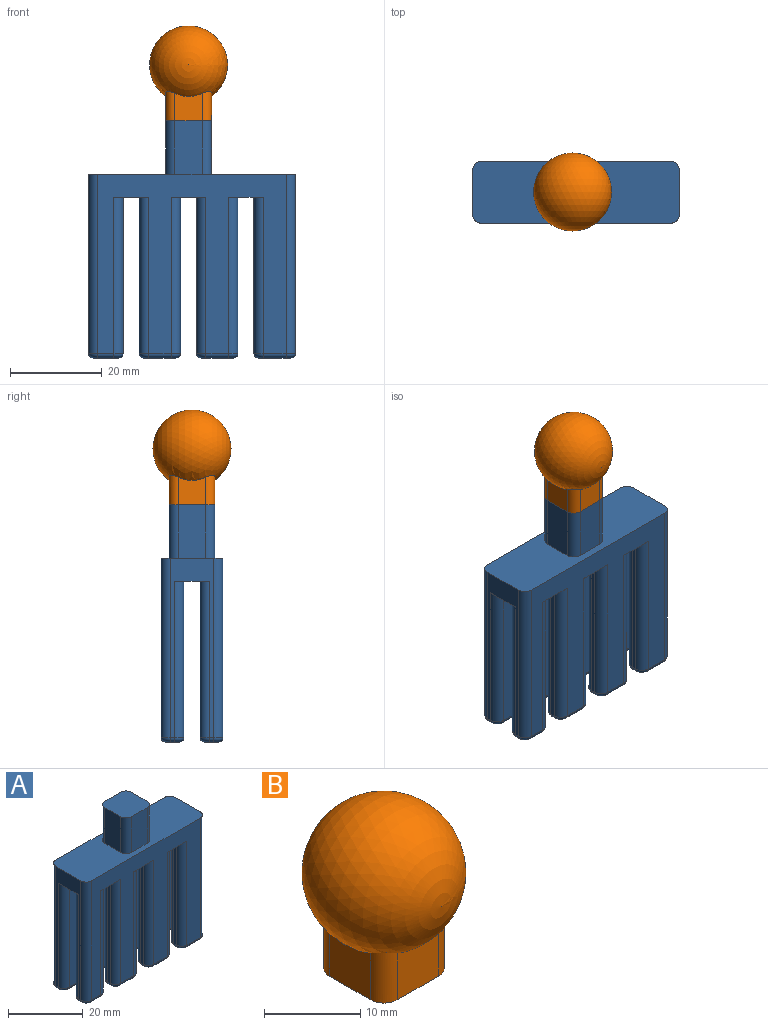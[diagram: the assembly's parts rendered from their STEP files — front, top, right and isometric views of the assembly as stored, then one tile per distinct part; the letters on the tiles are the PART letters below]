
ASSEMBLY  parts=2 mates=1
PART A: 139 faces, bbox 45.3x13.8x51.7 mm
  f0: plane 34x1mm, normal (-1,0,0), area 34mm2, adj f5,f26,f67,f92
  f1: plane 34x1mm, normal (-1,0,0), area 34mm2, adj f7,f26,f74,f77
  f2: plane 34x1mm, normal (1,0,0), area 34mm2, adj f4,f26,f65,f101
  f3: plane 34x1mm, normal (1,0,0), area 34mm2, adj f6,f26,f70,f84
  f4: cylinder r=2mm len=34mm, axis (0,0,1), area 106.8mm2, adj f2,f22,f26,f99
  f5: cylinder r=2mm len=34mm, axis (0,0,-1), area 106.8mm2, adj f0,f22,f26,f91
  f6: cylinder r=2mm len=34mm, axis (0,0,-1), area 106.8mm2, adj f3,f17,f26,f83
  f7: cylinder r=2mm len=34mm, axis (0,0,1), area 106.8mm2, adj f1,f17,f26,f75
  f8: plane 11.69x6mm, normal (-1,0,0), area 70.1mm2, adj f11,f14,f25,f32
  f9: plane 11.69x6mm, normal (1,0,0), area 70.1mm2, adj f12,f13,f25,f32
  f10: plane 11.69x6mm, normal (0,1,0), area 70.1mm2, adj f13,f14,f25,f32
  f11: cylinder r=2mm len=11.69mm, axis (0,0,-1), area 36.7mm2, adj f8,f25,f27,f32
  f12: cylinder r=2mm len=11.69mm, axis (0,0,1), area 36.7mm2, adj f9,f25,f27,f32
  f13: cylinder r=2mm len=11.69mm, axis (0,0,-1), area 36.7mm2, adj f9,f10,f25,f32
  f14: cylinder r=2mm len=11.69mm, axis (0,0,1), area 36.7mm2, adj f8,f10,f25,f32
  f15: plane 34x5mm, normal (0,-1,0), area 170mm2, adj f26,f72,f74,f81
  f16: plane 34x1mm, normal (1,0,0), area 34mm2, adj f26,f72,f73,f80
  f17: plane 41x39mm, normal (0,1,0), area 834mm2, adj f6,f7,f25,f26,f52,f53,f60,f62
  f18: plane 34x1mm, normal (-1,0,0), area 34mm2, adj f26,f69,f71,f89
  f19: plane 34x5mm, normal (0,-1,0), area 170mm2, adj f26,f69,f70,f88
  f20: plane 34x1mm, normal (1,0,0), area 34mm2, adj f26,f66,f68,f97
  f21: plane 34x5mm, normal (0,1,0), area 170mm2, adj f26,f66,f67,f96
  f22: plane 41x39mm, normal (0,-1,0), area 834mm2, adj f4,f5,f25,f26,f49,f58,f59,f61
  f23: plane 34x5mm, normal (0,1,0), area 170mm2, adj f26,f63,f65,f105
  f24: plane 34x1mm, normal (-1,0,0), area 34mm2, adj f26,f63,f64,f104
  f25: plane 45x13.5mm, normal (0,0,1), area 507.5mm2, adj f8,f9,f10,f11,f12,f13,f14,f17
  f26: plane 45x13.5mm, normal (0,0,-1), area 286.5mm2, adj f0,f1,f2,f3,f4,f5,f6,f7
  f27: plane 11.69x6mm, normal (0,-1,0), area 70.1mm2, adj f11,f12,f25,f32
  f28: plane 7x3mm, normal (0,0,-1), area 20.1mm2, adj f99,f100,f101,f102,f103,f104,f105,f106
  f29: plane 7x3mm, normal (0,0,-1), area 20.1mm2, adj f91,f92,f93,f94,f95,f96,f97,f98
  f30: plane 7x3mm, normal (0,0,-1), area 20.1mm2, adj f75,f76,f77,f78,f79,f80,f81,f82
  f31: plane 7x3mm, normal (0,0,-1), area 20.1mm2, adj f83,f84,f85,f86,f87,f88,f89,f90
  f32: plane 10x10mm, normal (0,0,1), area 96.6mm2, adj f8,f9,f10,f11,f12,f13,f14,f27
  f33: plane 39x9.5mm, normal (-1,0,0), area 115.5mm2, adj f25,f26,f48,f50,f59,f60,f129,f132
  f34: plane 39x9.5mm, normal (1,0,0), area 115.5mm2, adj f25,f26,f54,f56,f61,f62,f113,f117
  f35: plane 34x1mm, normal (-1,0,0), area 34mm2, adj f26,f57,f58,f108
  f36: plane 34x5mm, normal (0,1,0), area 170mm2, adj f26,f56,f57,f112
  f37: plane 7x3mm, normal (0,0,-1), area 20.1mm2, adj f107,f108,f109,f110,f111,f112,f113,f114
  f38: plane 34x1mm, normal (-1,0,0), area 34mm2, adj f26,f53,f55,f120
  f39: plane 34x5mm, normal (0,-1,0), area 170mm2, adj f26,f54,f55,f116
  f40: plane 7x3mm, normal (0,0,-1), area 20.1mm2, adj f115,f116,f117,f118,f119,f120,f121,f122
  f41: plane 34x1mm, normal (1,0,0), area 34mm2, adj f26,f47,f49,f137
  f42: plane 34x3.5mm, normal (0,1,0), area 119mm2, adj f26,f47,f48,f136
  f43: plane 5.5x3mm, normal (0,0,-1), area 15.6mm2, adj f131,f132,f133,f134,f135,f136,f137,f138
  f44: plane 34x1mm, normal (1,0,0), area 34mm2, adj f26,f51,f52,f124
  f45: plane 34x3.5mm, normal (0,-1,0), area 119mm2, adj f26,f50,f51,f128
  f46: plane 5.5x3mm, normal (0,0,-1), area 15.6mm2, adj f123,f124,f125,f126,f127,f128,f129,f130
  f47: cylinder r=2mm len=34mm, axis (0,0,-1), area 106.8mm2, adj f26,f41,f42,f138
  f48: cylinder r=2mm len=34mm, axis (0,0,1), area 106.8mm2, adj f26,f33,f42,f134
  f49: cylinder r=2mm len=34mm, axis (0,0,1), area 106.8mm2, adj f22,f26,f41,f135
  f50: cylinder r=2mm len=34mm, axis (0,0,-1), area 106.8mm2, adj f26,f33,f45,f130
  f51: cylinder r=2mm len=34mm, axis (0,0,-1), area 106.8mm2, adj f26,f44,f45,f126
  f52: cylinder r=2mm len=34mm, axis (0,0,1), area 106.8mm2, adj f17,f26,f44,f123
  f53: cylinder r=2mm len=34mm, axis (0,0,-1), area 106.8mm2, adj f17,f26,f38,f122
  f54: cylinder r=2mm len=34mm, axis (0,0,-1), area 106.8mm2, adj f26,f34,f39,f115
  f55: cylinder r=2mm len=34mm, axis (0,0,-1), area 106.8mm2, adj f26,f38,f39,f118
  f56: cylinder r=2mm len=34mm, axis (0,0,1), area 106.8mm2, adj f26,f34,f36,f114
  f57: cylinder r=2mm len=34mm, axis (0,0,-1), area 106.8mm2, adj f26,f35,f36,f110
  f58: cylinder r=2mm len=34mm, axis (0,0,-1), area 106.8mm2, adj f22,f26,f35,f107
  f59: cylinder r=2mm len=39mm, axis (0,0,1), area 122.5mm2, adj f22,f25,f33,f131
  f60: cylinder r=2mm len=39mm, axis (0,0,-1), area 122.5mm2, adj f17,f25,f33,f127
  f61: cylinder r=2mm len=39mm, axis (0,0,-1), area 122.5mm2, adj f22,f25,f34,f111
  f62: cylinder r=2mm len=39mm, axis (0,0,1), area 122.5mm2, adj f17,f25,f34,f119
  f63: cylinder r=2mm len=34mm, axis (0,0,1), area 106.8mm2, adj f23,f24,f26,f106
  f64: cylinder r=2mm len=34mm, axis (0,0,1), area 106.8mm2, adj f22,f24,f26,f102
  f65: cylinder r=2mm len=34mm, axis (0,0,1), area 106.8mm2, adj f2,f23,f26,f103
  f66: cylinder r=2mm len=34mm, axis (0,0,1), area 106.8mm2, adj f20,f21,f26,f98
  f67: cylinder r=2mm len=34mm, axis (0,0,1), area 106.8mm2, adj f0,f21,f26,f94
  f68: cylinder r=2mm len=34mm, axis (0,0,-1), area 106.8mm2, adj f20,f22,f26,f95
  f69: cylinder r=2mm len=34mm, axis (0,0,1), area 106.8mm2, adj f18,f19,f26,f90
  f70: cylinder r=2mm len=34mm, axis (0,0,-1), area 106.8mm2, adj f3,f19,f26,f86
  f71: cylinder r=2mm len=34mm, axis (0,0,1), area 106.8mm2, adj f17,f18,f26,f87
  f72: cylinder r=2mm len=34mm, axis (0,0,1), area 106.8mm2, adj f15,f16,f26,f82
  f73: cylinder r=2mm len=34mm, axis (0,0,-1), area 106.8mm2, adj f16,f17,f26,f78
  f74: cylinder r=2mm len=34mm, axis (0,0,-1), area 106.8mm2, adj f1,f15,f26,f79
  f75: torus R=1mm, axis (0,0,1), area 4mm2, adj f7,f30,f76,f77
  f76: cylinder r=1mm len=5mm, axis (-1,0,0), area 7.9mm2, adj f17,f30,f75,f78
  f77: cylinder r=1mm len=1mm, axis (0,-1,0), area 1.6mm2, adj f1,f30,f75,f79
  f78: torus R=1mm, axis (0,0,1), area 4mm2, adj f30,f73,f76,f80
  f79: torus R=1mm, axis (0,0,1), area 4mm2, adj f30,f74,f77,f81
  f80: cylinder r=1mm len=1mm, axis (0,1,0), area 1.6mm2, adj f16,f30,f78,f82
  f81: cylinder r=1mm len=5mm, axis (1,0,0), area 7.9mm2, adj f15,f30,f79,f82
  f82: torus R=1mm, axis (0,0,1), area 4mm2, adj f30,f72,f80,f81
  f83: torus R=1mm, axis (0,0,1), area 4mm2, adj f6,f31,f84,f85
  f84: cylinder r=1mm len=1mm, axis (0,1,0), area 1.6mm2, adj f3,f31,f83,f86
  f85: cylinder r=1mm len=5mm, axis (1,0,0), area 7.9mm2, adj f17,f31,f83,f87
  f86: torus R=1mm, axis (0,0,1), area 4mm2, adj f31,f70,f84,f88
  f87: torus R=1mm, axis (0,0,1), area 4mm2, adj f31,f71,f85,f89
  f88: cylinder r=1mm len=5mm, axis (1,0,0), area 7.9mm2, adj f19,f31,f86,f90
  f89: cylinder r=1mm len=1mm, axis (0,-1,0), area 1.6mm2, adj f18,f31,f87,f90
  f90: torus R=1mm, axis (0,0,1), area 4mm2, adj f31,f69,f88,f89
  f91: torus R=1mm, axis (0,0,1), area 4mm2, adj f5,f29,f92,f93
  f92: cylinder r=1mm len=1mm, axis (0,1,0), area 1.6mm2, adj f0,f29,f91,f94
  f93: cylinder r=1mm len=5mm, axis (1,0,0), area 7.9mm2, adj f22,f29,f91,f95
  f94: torus R=1mm, axis (0,0,1), area 4mm2, adj f29,f67,f92,f96
  f95: torus R=1mm, axis (0,0,1), area 4mm2, adj f29,f68,f93,f97
  f96: cylinder r=1mm len=5mm, axis (-1,0,0), area 7.9mm2, adj f21,f29,f94,f98
  f97: cylinder r=1mm len=1mm, axis (0,1,0), area 1.6mm2, adj f20,f29,f95,f98
  f98: torus R=1mm, axis (0,0,1), area 4mm2, adj f29,f66,f96,f97
  f99: torus R=1mm, axis (0,0,1), area 4mm2, adj f4,f28,f100,f101
  f100: cylinder r=1mm len=5mm, axis (-1,0,0), area 7.9mm2, adj f22,f28,f99,f102
  f101: cylinder r=1mm len=1mm, axis (0,-1,0), area 1.6mm2, adj f2,f28,f99,f103
  f102: torus R=1mm, axis (0,0,1), area 4mm2, adj f28,f64,f100,f104
  f103: torus R=1mm, axis (0,0,1), area 4mm2, adj f28,f65,f101,f105
  f104: cylinder r=1mm len=1mm, axis (0,-1,0), area 1.6mm2, adj f24,f28,f102,f106
  f105: cylinder r=1mm len=5mm, axis (-1,0,0), area 7.9mm2, adj f23,f28,f103,f106
  f106: torus R=1mm, axis (0,0,1), area 4mm2, adj f28,f63,f104,f105
  f107: torus R=1mm, axis (0,0,-1), area 4mm2, adj f37,f58,f108,f109
  f108: cylinder r=1mm len=1mm, axis (0,-1,0), area 1.6mm2, adj f35,f37,f107,f110
  f109: cylinder r=1mm len=5mm, axis (-1,0,0), area 7.9mm2, adj f22,f37,f107,f111
  f110: torus R=1mm, axis (0,0,-1), area 4mm2, adj f37,f57,f108,f112
  f111: torus R=1mm, axis (0,0,-1), area 4mm2, adj f37,f61,f109,f113
  f112: cylinder r=1mm len=5mm, axis (-1,0,0), area 7.9mm2, adj f36,f37,f110,f114
  f113: cylinder r=1mm len=1mm, axis (0,1,0), area 1.6mm2, adj f34,f37,f111,f114
  f114: torus R=1mm, axis (0,0,-1), area 4mm2, adj f37,f56,f112,f113
  f115: torus R=1mm, axis (0,0,-1), area 4mm2, adj f40,f54,f116,f117
  f116: cylinder r=1mm len=5mm, axis (1,0,0), area 7.9mm2, adj f39,f40,f115,f118
  f117: cylinder r=1mm len=1mm, axis (0,1,0), area 1.6mm2, adj f34,f40,f115,f119
  f118: torus R=1mm, axis (0,0,-1), area 4mm2, adj f40,f55,f116,f120
  f119: torus R=1mm, axis (0,0,-1), area 4mm2, adj f40,f62,f117,f121
  f120: cylinder r=1mm len=1mm, axis (0,-1,0), area 1.6mm2, adj f38,f40,f118,f122
  f121: cylinder r=1mm len=5mm, axis (1,0,0), area 7.9mm2, adj f17,f40,f119,f122
  f122: torus R=1mm, axis (0,0,-1), area 4mm2, adj f40,f53,f120,f121
  f123: torus R=1mm, axis (0,0,-1), area 4mm2, adj f46,f52,f124,f125
  f124: cylinder r=1mm len=1mm, axis (0,1,0), area 1.6mm2, adj f44,f46,f123,f126
  f125: cylinder r=1mm len=3.5mm, axis (1,0,0), area 5.5mm2, adj f17,f46,f123,f127
  f126: torus R=1mm, axis (0,0,-1), area 4mm2, adj f46,f51,f124,f128
  f127: torus R=1mm, axis (0,0,-1), area 4mm2, adj f46,f60,f125,f129
  f128: cylinder r=1mm len=3.5mm, axis (1,0,0), area 5.5mm2, adj f45,f46,f126,f130
  f129: cylinder r=1mm len=1mm, axis (0,-1,0), area 1.6mm2, adj f33,f46,f127,f130
  f130: torus R=1mm, axis (0,0,-1), area 4mm2, adj f46,f50,f128,f129
  f131: torus R=1mm, axis (0,0,-1), area 4mm2, adj f43,f59,f132,f133
  f132: cylinder r=1mm len=1mm, axis (0,-1,0), area 1.6mm2, adj f33,f43,f131,f134
  f133: cylinder r=1mm len=3.5mm, axis (-1,0,0), area 5.5mm2, adj f22,f43,f131,f135
  f134: torus R=1mm, axis (0,0,-1), area 4mm2, adj f43,f48,f132,f136
  f135: torus R=1mm, axis (0,0,-1), area 4mm2, adj f43,f49,f133,f137
  f136: cylinder r=1mm len=3.5mm, axis (-1,0,0), area 5.5mm2, adj f42,f43,f134,f138
  f137: cylinder r=1mm len=1mm, axis (0,1,0), area 1.6mm2, adj f41,f43,f135,f138
  f138: torus R=1mm, axis (0,0,-1), area 4mm2, adj f43,f47,f136,f137
PART B: 10 faces, bbox 17x17x20.6 mm
  f0: sphere r=8.5mm, area 797.4mm2, adj f1,f2,f3,f4,f5,f6,f7,f8
  f1: cylinder r=2mm len=6.38mm, axis (0,0,-1), area 19.6mm2, adj f0,f7,f8,f9
  f2: cylinder r=2mm len=6.38mm, axis (0,0,1), area 19.6mm2, adj f0,f6,f8,f9
  f3: cylinder r=2mm len=6.38mm, axis (0,0,-1), area 19.6mm2, adj f0,f5,f6,f9
  f4: cylinder r=2mm len=6.38mm, axis (0,0,1), area 19.6mm2, adj f0,f5,f7,f9
  f5: plane 6x5.96mm, normal (0,1,0), area 33mm2, adj f0,f3,f4,f9
  f6: plane 6x5.96mm, normal (1,0,0), area 33mm2, adj f0,f2,f3,f9
  f7: plane 6x5.96mm, normal (-1,0,0), area 33mm2, adj f0,f1,f4,f9
  f8: plane 6x5.96mm, normal (0,-1,0), area 33mm2, adj f0,f1,f2,f9
  f9: plane 10x10mm, normal (0,0,-1), area 96.6mm2, adj f1,f2,f3,f4,f5,f6,f7,f8
PLACE A t=(0.29,-0.09,-13.87)mm
PLACE B t=(0.29,-0.09,-20.04)mm
MATE fastened B.f9 <-> A.f32  axis (0,0,-1) through (2.04,-1.84,22.82)mm
